FCSTD DOCUMENT  (FreeCAD 0.17R11939 (Git))
Label: buck_chuck_lever
License: All rights reserved
LicenseURL: http://en.wikipedia.org/wiki/All_rights_reserved
objects: Sketcher::SketchObject×1
note: 1 computed .brp shape members not serialized (recipe doc carries the construction recipe); baked Part::Feature solids carry a one-line shape summary decoded from their .brp

FEATURE [Sketcher::SketchObject] Sketch
  sketch-geometry (16):
    g0: LineSegment StartX=-9.38 StartY=0 StartZ=0 EndX=-9.38 EndY=4 EndZ=0
    g1: LineSegment StartX=-9.38 StartY=4 StartZ=0 EndX=-5.4 EndY=4 EndZ=0
    g2: LineSegment StartX=-5.4 StartY=4 StartZ=0 EndX=-5.4 EndY=11.9375 EndZ=0
    g3: LineSegment StartX=5.4 StartY=11.9375 StartZ=0 EndX=5.4 EndY=4 EndZ=0
    g4: LineSegment StartX=5.4 StartY=4 StartZ=0 EndX=9.38 EndY=4 EndZ=0
    g5: LineSegment StartX=9.38 StartY=4 StartZ=0 EndX=9.38 EndY=0 EndZ=0
    g6: LineSegment StartX=9.38 StartY=0 StartZ=0 EndX=-9.38 EndY=0 EndZ=0
    g7: LineSegment StartX=-5.4 StartY=11.9375 StartZ=0 EndX=-9.38 EndY=11.9375 EndZ=0
    g8: LineSegment StartX=-9.38 StartY=11.9375 StartZ=0 EndX=-9.38 EndY=19 EndZ=0
    g9: LineSegment StartX=5.4 StartY=11.9375 StartZ=0 EndX=9.38 EndY=11.9375 EndZ=0
    g10: LineSegment StartX=9.38 StartY=11.9375 StartZ=0 EndX=9.38 EndY=19 EndZ=0
    g11: LineSegment StartX=9.38 StartY=19 StartZ=0 EndX=-9.38 EndY=19 EndZ=0
    g12: LineSegment StartX=-9.38 StartY=0 StartZ=0 EndX=-9.62 EndY=0 EndZ=0
    g13: LineSegment StartX=-9.62 StartY=0 StartZ=0 EndX=-9.62 EndY=19 EndZ=0
    g14: LineSegment StartX=-9.62 StartY=19 StartZ=0 EndX=-9.38 EndY=19 EndZ=0
    g15: GeomPoint X=-5.4 Y=7.96875 Z=0
  constraints (50):
    c: PointOnObject(g0,g-1)
    c: Vertical(g0)
    c: Coincident(g0,g1)
    c: Coincident(g1,g2)
    c: Vertical(g2)
    c: Vertical(g3)
    c: Coincident(g3,g4)
    c: Horizontal(g4)
    c: Coincident(g4,g5)
    c: PointOnObject(g5,g-1)
    c: Vertical(g5)
    c: Coincident(g5,g6)
    c: Coincident(g6,g0)
    c: Horizontal(g1)
    c: Equal(g1,g4)
    c: Distance(g6) = 18.76
    c: Distance(g0) = 4
    c: Horizontal(g7)
    c: Coincident(g8,g7)
    c: Vertical(g8)
    c: Coincident(g2,g7)
    c: Horizontal(g9)
    c: Coincident(g10,g9)
    c: Vertical(g10)
    c: Horizontal(g11)
    c: Coincident(g10,g11)
    c: Equal(g9,g7)
    c: Coincident(g3,g9)
    c: Equal(g3,g2)
    c: Equal(g5,g0)
    c: Coincident(g8,g11)
    c: DistanceY(g0,g8) = 19
    c: DistanceX(g2,g3) = 10.8
    c: Equal(g11,g6)
    c: Distance(g2) = 7.9375
    c: DistanceX(g7,g7) = 3.98
    c: Symmetric(g0,g5,g-2)
    c: Coincident(g12,g0)
    c: Horizontal(g12)
    c: Coincident(g13,g12)
    c: Vertical(g13)
    c: Coincident(g14,g13)
    c: Coincident(g14,g8)
    c: Horizontal(g14)
    c: DistanceX(g12,g5) = 19
    c: DistanceX(g14,g14) = 0.24
    c: PointOnObject(g15,g2)
    c: Symmetric(g1,g2,g15)
    c: DistanceY(g-1,g15) = 7.96875
    c: DistanceY(g15,g8) = 11.0312
